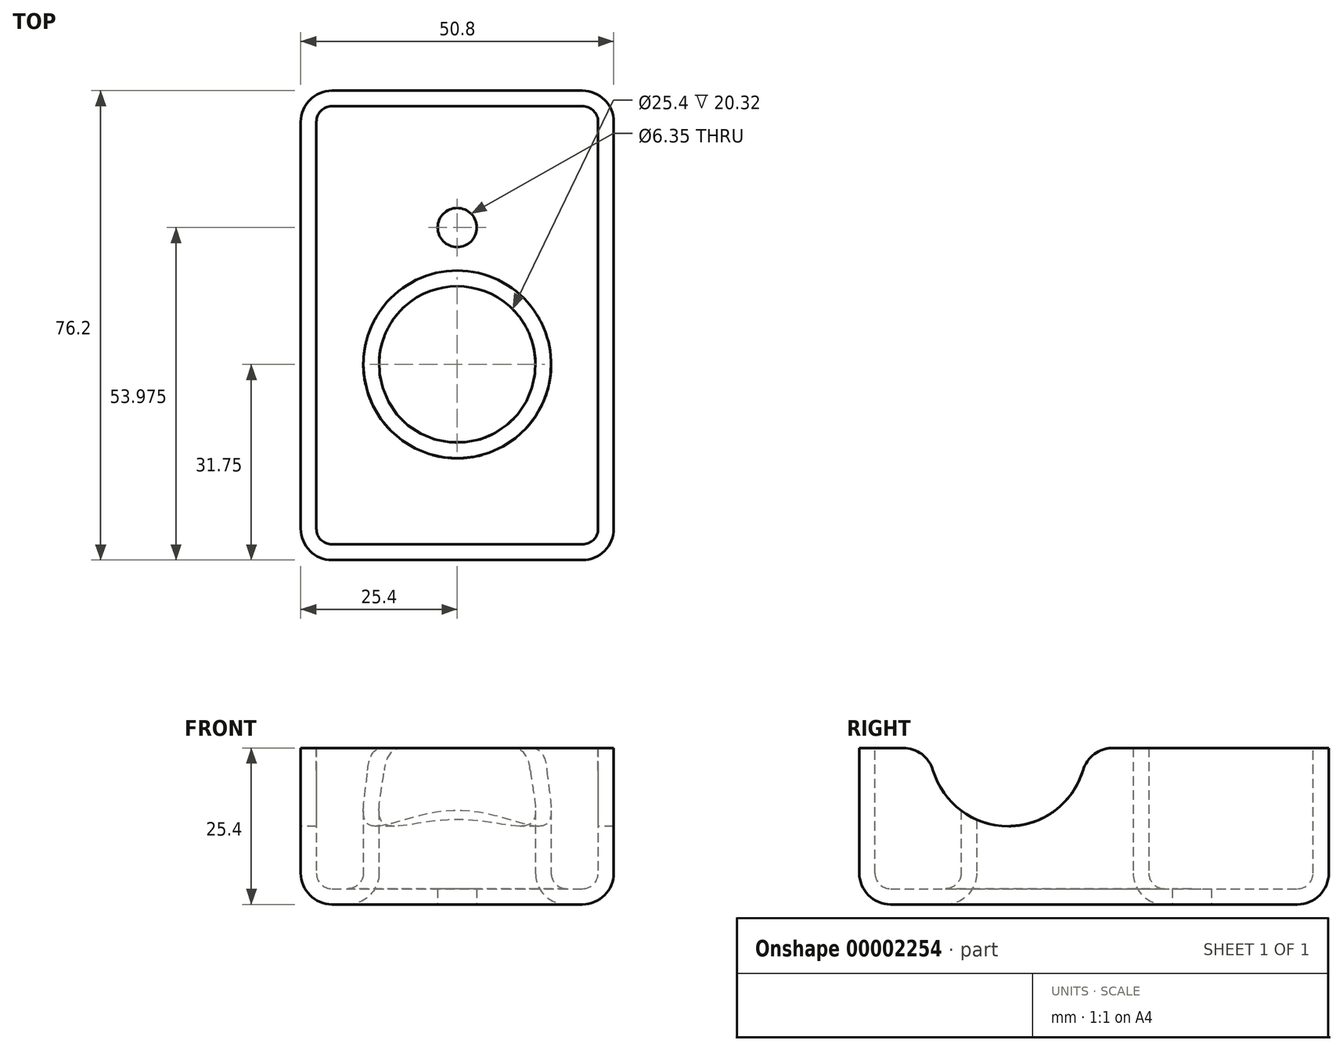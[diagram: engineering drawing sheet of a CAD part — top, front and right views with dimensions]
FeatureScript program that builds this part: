
annotation { "Feature Type Name" : "Feature", "Feature Type Description" : "" }
export const myFeature = defineFeature(function(context is Context, id is Id, definition is map)
    precondition{}
    {
        {
            var Q0;
            Q0=qCreatedBy(makeId("Top.planeOp"),FACE);
            var sketch = newSketch(context, id + "F0", { "sketchPlane" : qUnion([Q0])});
            skLineSegment(sketch, "E0.bottom", {"start": v(-50.8, 76.2) * mm, "end": v(0, 76.2) * mm});
            skLineSegment(sketch, "E0.top", {"start": v(-50.8, 0) * mm, "end": v(0, 0) * mm});
            skLineSegment(sketch, "E0.left", {"start": v(-50.8, 76.2) * mm, "end": v(-50.8, 0) * mm});
            skLineSegment(sketch, "E0.right", {"start": v(0, 76.2) * mm, "end": v(0, 0) * mm});
            skCircle(sketch, "E1", {"center": v(-25.4, 31.75) * mm, "radius": 12.7 * mm});
            skSolve(sketch);
        }
        {
            var Q0;
            Q0=makeQuery(id+"F0.imprint","IMPRINT",FACE,{"disambiguationData":[TD([[makeQuery(id+"F0.imprint","IMPRINT",EDGE,{"derivedFrom":sQuery(id+"F0.wireOp",EDGE,"E0.bottom")}),-1.0]])]});
            extrude(context, id + "F1", {"entities" : qUnion([Q0]), "depth" : 25.4 * mm});
        }
        {
            var Q0;
            Q0=makeQuery(id+"F1.opExtrude","SWEPT_EDGE",EDGE,{"disambiguationData":[OSD([sQuery(id+"F0.wireOp",EDGE,"E0.bottom"),sQuery(id+"F0.wireOp",EDGE,"E0.left")])]});
            var Q1;
            Q1=makeQuery(id+"F1.opExtrude","SWEPT_EDGE",EDGE,{"disambiguationData":[OSD([sQuery(id+"F0.wireOp",EDGE,"E0.bottom"),sQuery(id+"F0.wireOp",EDGE,"E0.right")])]});
            var Q2;
            Q2=makeQuery(id+"F1.opExtrude","SWEPT_EDGE",EDGE,{"disambiguationData":[OSD([sQuery(id+"F0.wireOp",EDGE,"E0.top"),sQuery(id+"F0.wireOp",EDGE,"E0.right")])]});
            var Q3;
            Q3=makeQuery(id+"F1.opExtrude","SWEPT_EDGE",EDGE,{"disambiguationData":[OSD([sQuery(id+"F0.wireOp",EDGE,"E0.top"),sQuery(id+"F0.wireOp",EDGE,"E0.left")])]});
            var Q4;
            Q4=makeQuery(id+"F1.opExtrude","CAP_FACE",FACE,{"disambiguationData":[OSD([sQuery(id+"F0.wireOp",EDGE,"E0.bottom"),sQuery(id+"F0.wireOp",EDGE,"E0.top"),sQuery(id+"F0.wireOp",EDGE,"E0.left"),sQuery(id+"F0.wireOp",EDGE,"E0.right"),sQuery(id+"F0.wireOp",EDGE,"E1")])],"isStart":true});
            fillet(context, id + "F2", {"entities" : qUnion([Q0, Q1, Q2, Q3, Q4]), "radius" : 5.08 * mm, "tangentPropagation" : true, "allowEdgeOverflow" : false});
        }
        {
            var Q0;
            Q0=makeQuery(id+"F1.opExtrude","CAP_FACE",FACE,{"disambiguationData":[OSD([sQuery(id+"F0.wireOp",EDGE,"E0.bottom"),sQuery(id+"F0.wireOp",EDGE,"E0.top"),sQuery(id+"F0.wireOp",EDGE,"E0.left"),sQuery(id+"F0.wireOp",EDGE,"E0.right"),sQuery(id+"F0.wireOp",EDGE,"E1")])],"isStart":false});
            shell(context, id + "F3", {"entities" : qUnion([Q0]), "thickness" : 2.54 * mm});
        }
        {
            var Q0;
            Q0=makeQuery(id+"F1.opExtrude","SWEPT_FACE",FACE,{"disambiguationData":[OSD([sQuery(id+"F0.wireOp",EDGE,"E0.left")])]});
            var sketch = newSketch(context, id + "F4", { "sketchPlane" : qUnion([Q0])});
            skCircle(sketch, "E2", {"center": v(-24.13, 25.4) * mm, "radius": 12.7 * mm});
            skSolve(sketch);
        }
        {
            var Q0;
            {var subQ0=makeQuery(id+"F1.opExtrude","CAP_EDGE",EDGE,{"disambiguationData":[OSD([sQuery(id+"F0.wireOp",EDGE,"E0.left")])],"isStart":false});var subQ1=sQuery(id+"F4.wireOp",EDGE,"E2");var subQ3=makeQuery(id+"F4.imprint","INTERSECT",VERTEX,{"disambiguationData":[OD(0.0)],"derivedFrom":[subQ0,subQ1]});Q0=qUnion([makeQuery(id+"F4.imprint","IMPRINT",FACE,{"disambiguationData":[TD([[makeQuery(id+"F4.imprint","IMPRINT",EDGE,{"disambiguationData":[TD([[subQ3,1.0]])],"derivedFrom":subQ1}),1.0]])]}),makeQuery(id+"F4.imprint","IMPRINT",FACE,{"disambiguationData":[TD([[makeQuery(id+"F4.imprint","IMPRINT",EDGE,{"disambiguationData":[TD([[subQ3,-1.0]])],"derivedFrom":subQ1}),1.0]])]})]);}
            extrude(context, id + "F5", {"entities" : qUnion([Q0]), "operationType" : NewBodyOperationType.REMOVE, "endBound" : BoundingType.THROUGH_ALL, "oppositeDirection" : true, "depth" : 25.4 * mm});
        }
        {
            var Q0;
            {var subQ0=sQuery(id+"F0.wireOp",EDGE,"E0.bottom");var subQ1=sQuery(id+"F0.wireOp",EDGE,"E0.top");var subQ2=sQuery(id+"F0.wireOp",EDGE,"E0.left");var subQ3=sQuery(id+"F0.wireOp",EDGE,"E0.right");var subQ4=sQuery(id+"F0.wireOp",EDGE,"E1");Q0=makeQuery(id+"F5.boolean.opBoolean","INTERSECT",EDGE,{"disambiguationData":[OD(0.0)],"derivedFrom":[makeQuery(id+"F3.opShell","OFFSET_FACE",FACE,{"disambiguationData":[OSD([subQ0,subQ1,subQ2,subQ3,subQ4]),TDD([makeQuery(id+"F1.opExtrude","CAP_FACE",FACE,{"disambiguationData":[OSD([subQ0,subQ1,subQ2,subQ3,subQ4])],"isStart":false})])]}),makeQuery(id+"F5.opExtrude","SWEPT_FACE",FACE,{"disambiguationData":[OSD([sQuery(id+"F4.wireOp",EDGE,"E2")])]})]});}
            var Q1;
            Q1=makeQuery(id+"F5.boolean.opBoolean","INTERSECT",EDGE,{"disambiguationData":[OD(0.0)],"derivedFrom":[makeQuery(id+"F1.opExtrude","CAP_FACE",FACE,{"disambiguationData":[OSD([sQuery(id+"F0.wireOp",EDGE,"E0.bottom"),sQuery(id+"F0.wireOp",EDGE,"E0.top"),sQuery(id+"F0.wireOp",EDGE,"E0.left"),sQuery(id+"F0.wireOp",EDGE,"E0.right"),sQuery(id+"F0.wireOp",EDGE,"E1")])],"isStart":false}),makeQuery(id+"F5.opExtrude","SWEPT_FACE",FACE,{"disambiguationData":[OSD([sQuery(id+"F4.wireOp",EDGE,"E2")])]})]});
            var Q2;
            {var subQ0=sQuery(id+"F0.wireOp",EDGE,"E0.bottom");var subQ1=sQuery(id+"F0.wireOp",EDGE,"E0.top");var subQ2=sQuery(id+"F0.wireOp",EDGE,"E0.left");var subQ3=sQuery(id+"F0.wireOp",EDGE,"E0.right");var subQ4=sQuery(id+"F0.wireOp",EDGE,"E1");Q2=makeQuery(id+"F5.boolean.opBoolean","INTERSECT",EDGE,{"disambiguationData":[OD(2.0)],"derivedFrom":[makeQuery(id+"F3.opShell","OFFSET_FACE",FACE,{"disambiguationData":[OSD([subQ0,subQ1,subQ2,subQ3,subQ4]),TDD([makeQuery(id+"F1.opExtrude","CAP_FACE",FACE,{"disambiguationData":[OSD([subQ0,subQ1,subQ2,subQ3,subQ4])],"isStart":false})])]}),makeQuery(id+"F5.opExtrude","SWEPT_FACE",FACE,{"disambiguationData":[OSD([sQuery(id+"F4.wireOp",EDGE,"E2")])]})]});}
            var Q3;
            Q3=makeQuery(id+"F5.boolean.opBoolean","INTERSECT",EDGE,{"disambiguationData":[OD(1.0)],"derivedFrom":[makeQuery(id+"F1.opExtrude","CAP_FACE",FACE,{"disambiguationData":[OSD([sQuery(id+"F0.wireOp",EDGE,"E0.bottom"),sQuery(id+"F0.wireOp",EDGE,"E0.top"),sQuery(id+"F0.wireOp",EDGE,"E0.left"),sQuery(id+"F0.wireOp",EDGE,"E0.right"),sQuery(id+"F0.wireOp",EDGE,"E1")])],"isStart":false}),makeQuery(id+"F5.opExtrude","SWEPT_FACE",FACE,{"disambiguationData":[OSD([sQuery(id+"F4.wireOp",EDGE,"E2")])]})]});
            var Q4;
            {var subQ0=sQuery(id+"F0.wireOp",EDGE,"E0.bottom");var subQ1=sQuery(id+"F0.wireOp",EDGE,"E0.top");var subQ2=sQuery(id+"F0.wireOp",EDGE,"E0.left");var subQ3=sQuery(id+"F0.wireOp",EDGE,"E0.right");var subQ4=sQuery(id+"F0.wireOp",EDGE,"E1");Q4=makeQuery(id+"F5.boolean.opBoolean","INTERSECT",EDGE,{"disambiguationData":[OD(1.0)],"derivedFrom":[makeQuery(id+"F3.opShell","OFFSET_FACE",FACE,{"disambiguationData":[OSD([subQ0,subQ1,subQ2,subQ3,subQ4]),TDD([makeQuery(id+"F1.opExtrude","CAP_FACE",FACE,{"disambiguationData":[OSD([subQ0,subQ1,subQ2,subQ3,subQ4])],"isStart":false})])]}),makeQuery(id+"F5.opExtrude","SWEPT_FACE",FACE,{"disambiguationData":[OSD([sQuery(id+"F4.wireOp",EDGE,"E2")])]})]});}
            var Q5;
            {var subQ0=sQuery(id+"F0.wireOp",EDGE,"E0.bottom");var subQ1=sQuery(id+"F0.wireOp",EDGE,"E0.top");var subQ2=sQuery(id+"F0.wireOp",EDGE,"E0.left");var subQ3=sQuery(id+"F0.wireOp",EDGE,"E0.right");var subQ4=sQuery(id+"F0.wireOp",EDGE,"E1");Q5=makeQuery(id+"F5.boolean.opBoolean","INTERSECT",EDGE,{"disambiguationData":[OD(3.0)],"derivedFrom":[makeQuery(id+"F3.opShell","OFFSET_FACE",FACE,{"disambiguationData":[OSD([subQ0,subQ1,subQ2,subQ3,subQ4]),TDD([makeQuery(id+"F1.opExtrude","CAP_FACE",FACE,{"disambiguationData":[OSD([subQ0,subQ1,subQ2,subQ3,subQ4])],"isStart":false})])]}),makeQuery(id+"F5.opExtrude","SWEPT_FACE",FACE,{"disambiguationData":[OSD([sQuery(id+"F4.wireOp",EDGE,"E2")])]})]});}
            fillet(context, id + "F6", {"entities" : qUnion([Q0, Q1, Q2, Q3, Q4, Q5]), "radius" : 5.08 * mm, "tangentPropagation" : true, "allowEdgeOverflow" : false});
        }
        {
            var Q0;
            Q0=makeQuery(id+"F1.opExtrude","CAP_FACE",FACE,{"disambiguationData":[OSD([sQuery(id+"F0.wireOp",EDGE,"E0.bottom"),sQuery(id+"F0.wireOp",EDGE,"E0.top"),sQuery(id+"F0.wireOp",EDGE,"E0.left"),sQuery(id+"F0.wireOp",EDGE,"E0.right"),sQuery(id+"F0.wireOp",EDGE,"E1")])],"isStart":true});
            var sketch = newSketch(context, id + "F7", { "sketchPlane" : qUnion([Q0])});
            skCircle(sketch, "E3", {"center": v(-25.4, -53.98) * mm, "radius": 3.18 * mm});
            skSolve(sketch);
        }
        {
            var Q0;
            Q0 = qSketchRegion(id + "F7", true);
            extrude(context, id + "F8", {"entities" : qUnion([Q0]), "operationType" : NewBodyOperationType.REMOVE, "endBound" : BoundingType.THROUGH_ALL, "oppositeDirection" : true, "depth" : 25.4 * mm});
        }
    });
